# Revit family: LAMP_LUP WALL 70 DIRECT
name_source: partatom
category: Luminarias
revit_build: Autodesk Revit 2018 (Build: 20190510_1515(x64)
units: mm (PartAtom-declared; Revit-internal decimal feet)

## family parameters
Anfitrión = Cara
Compartido = No
Corte con vacíos al cargar = No
Cota de conector redondo = Diámetro de uso
Origen de luz = Sí
Punto de cálculo de habitación = No
Tipo de pieza = Normal

## types (2) — shared parameters
CRI = 80
Cambio de temperatura de color de luz atenuada = <Ninguno>
Diameter = 70
Elevación por defecto = 1219 mm
Filtro de color = 16777215
Finish = Texturised black RAL 9011
Gear = Electronic
Height = 295
Installation instructions = https://www.lamp.es
Insulation class = I
LED Lifetime = 50.000 L80 B10
Lamp = COB LED
Last update = 10/02/2022
MacAdam = 3
Manufacturer URL = http://www.lamp.es
Manufacturer country = Spain
Manufacturer name = LAMP
Material COB = LAMP_COB
Material cristal = LAMP_CRISTAL Aro Kombic
Material cuerpo = LAMP_Aluminio perfil Ocult NG
Material reflector = LAMP_Aluminio Reflector Imag
Plum = 11 W
Power = 9 W
Power Supply = 220-240V 50/60Hz
Product URL = https://www.lamp.es
Product datasheet = http://www.lamp.es
Protection rating = IP65 / IK06
Type = COB PHILIPS
Weight = 1.37 kg
Ángulo de inclinación = 0.00°

## per-type parameters (varying)
| type | Archivo de red fotométrica | Efficacy | Product code |
| 665LM 3000 ASYM BLACK | LW170DR10AS30NB.IES | 63 lm/W | LW170DR10AS30NB |
| 705LM 4000 ASYM BLACK | LW170DR10AS40NB.IES | 67 lm/W | LW170DR10AS40NB |
